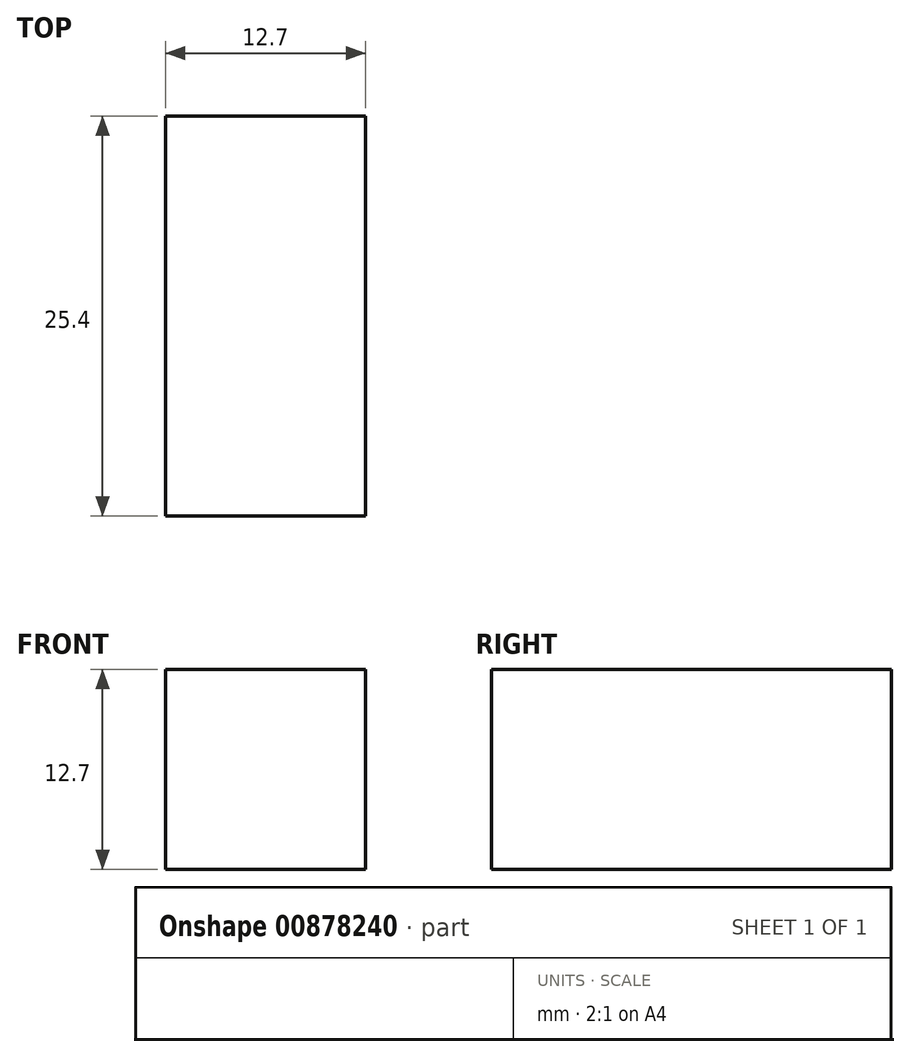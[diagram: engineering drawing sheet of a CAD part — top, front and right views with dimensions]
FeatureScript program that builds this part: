
annotation { "Feature Type Name" : "Feature", "Feature Type Description" : "" }
export const myFeature = defineFeature(function(context is Context, id is Id, definition is map)
    precondition{}
    {
        {
            var Q0;
            Q0=qCreatedBy(makeId("Top.planeOp"),FACE);
            var sketch = newSketch(context, id + "F0", { "sketchPlane" : qUnion([Q0])});
            skLineSegment(sketch, "E0.bottom", {"start": v(6.35, -12.7) * mm, "end": v(-6.35, -12.7) * mm});
            skLineSegment(sketch, "E0.top", {"start": v(6.35, 12.7) * mm, "end": v(-6.35, 12.7) * mm});
            skLineSegment(sketch, "E0.left", {"start": v(6.35, -12.7) * mm, "end": v(6.35, 12.7) * mm});
            skLineSegment(sketch, "E0.right", {"start": v(-6.35, -12.7) * mm, "end": v(-6.35, 12.7) * mm});
            skPoint(sketch, "E0.middle", {"position": v(0, 0) * mm});
            skSolve(sketch);
        }
        {
            var Q0;
            Q0=makeQuery(id+"F0.imprint","IMPRINT",FACE,{"disambiguationData":[TD([[makeQuery(id+"F0.imprint","IMPRINT",EDGE,{"derivedFrom":sQuery(id+"F0.wireOp",EDGE,"E0.bottom")}),-1.0]])]});
            extrude(context, id + "F1", {"entities" : qUnion([Q0]), "depth" : 12.7 * mm, "offsetDistance" : 25.4 * mm});
        }
    });
